# Revit family: ELVIRE 400 INSET BASIN NTH NOF
name_source: partatom
category: Plumbing Fixtures
revit_build: Autodesk Revit 2016 (Build: 20161004_0715(x64)
units: mm (PartAtom-declared; Revit-internal decimal feet)

## family parameters
Cut with Voids When Loaded = Yes
Host = Face
OmniClass Number = 23.45.05.14.14
OmniClass Title = Sinks/Lavatories
Part Type = Normal
Room Calculation Point = No
Round Connector Dimension = Use Diameter
Shared = No

## types (1)
- ELVIRE 400 INSET BASIN NTH NOF
    Assembly Code = D2010400
    CW Connection = No
    Default Elevation = 0 mm  [stored 0 ft]
    Description = ELVIRE 400 INSET BASIN NTH NOF
    HW Connection = No
    Manufacturer = GWA Bathrooms & Kitchens
    Material_Basin = GWA-Metalwork-White
    Material_Waste = GWA-Metalwork-White
    Model = CAEL0001W
    URL = https://www.caroma.com.au
    Vent Connection = No
    Waste Connection = Yes

note: [stored X ft] marks values corroborated as IEEE doubles in the binary element streams (Revit-internal decimal feet)

## geometry (parser evidence)
native form markers: Sweep x2
no freeform markers — native parametric forms only
